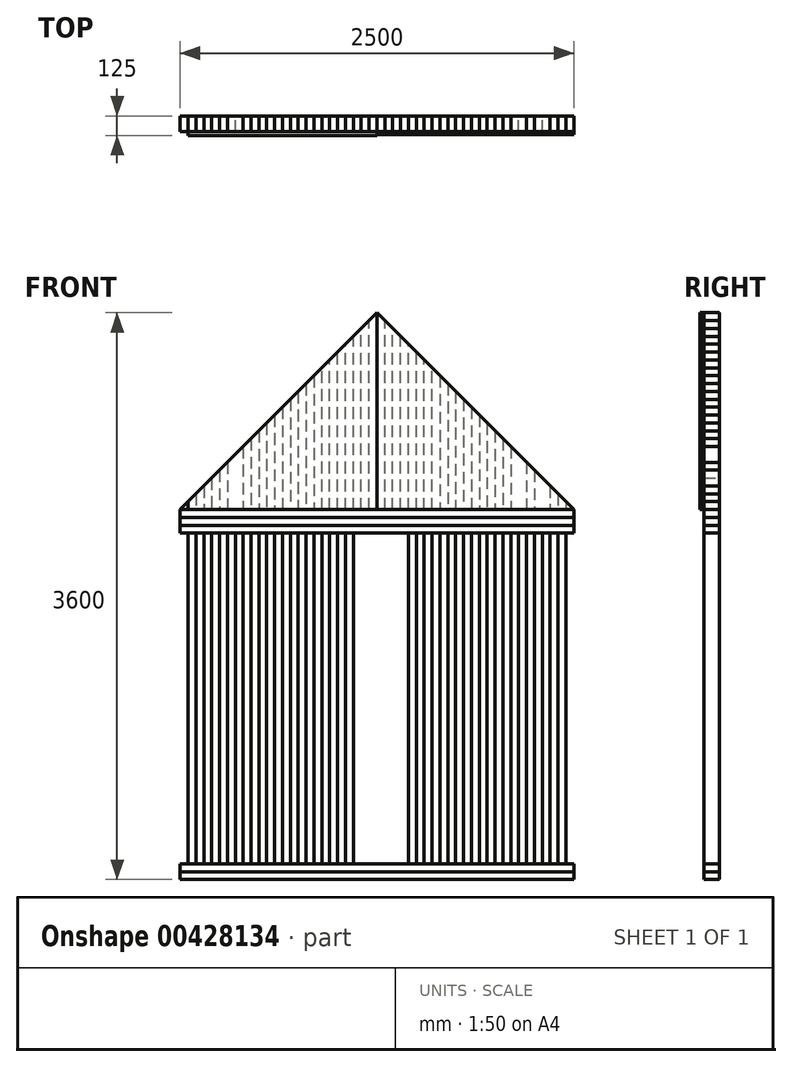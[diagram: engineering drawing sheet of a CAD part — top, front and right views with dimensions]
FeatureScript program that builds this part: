
annotation { "Feature Type Name" : "Feature", "Feature Type Description" : "" }
export const myFeature = defineFeature(function(context is Context, id is Id, definition is map)
    precondition{}
    {
        {
            var Q0;
            Q0=qCreatedBy(makeId("Front.planeOp"),FACE);
            var sketch = newSketch(context, id + "F0", { "sketchPlane" : qUnion([Q0])});
            skLineSegment(sketch, "E0.top", {"start": v(-1858, -1281.68) * mm, "end": v(642, -1281.68) * mm});
            skLineSegment(sketch, "E0.left", {"start": v(-1858, 1118.32) * mm, "end": v(-1858, -1281.68) * mm});
            skLineSegment(sketch, "E0.right", {"start": v(642, 1118.32) * mm, "end": v(642, -1281.68) * mm});
            skLineSegment(sketch, "E1", {"start": v(-1858, 1118.32) * mm, "end": v(-608, 2368.32) * mm});
            skLineSegment(sketch, "E2", {"start": v(-608, 2368.32) * mm, "end": v(642, 1118.32) * mm});
            skLineSegment(sketch, "E3.left", {"start": v(-1858, 1118.32) * mm, "end": v(-1858, 968.32) * mm});
            skLineSegment(sketch, "E3.right", {"start": v(642, 1118.32) * mm, "end": v(642, 968.32) * mm});
            skLineSegment(sketch, "E4", {"start": v(-1858, 1118.32) * mm, "end": v(642, 1118.32) * mm});
            skLineSegment(sketch, "E5", {"start": v(-608, 1118.32) * mm, "end": v(-608, 2368.32) * mm, "construction": true});
            skLineSegment(sketch, "E6", {"start": v(-608, 1118.32) * mm, "end": v(-658, 1118.32) * mm});
            skLineSegment(sketch, "E7", {"start": v(-658, 1118.32) * mm, "end": v(-658, 2318.32) * mm});
            skLineSegment(sketch, "E8", {"start": v(-708, 1118.32) * mm, "end": v(-708, 2268.32) * mm});
            skLineSegment(sketch, "E9", {"start": v(-758, 1118.32) * mm, "end": v(-758, 2218.32) * mm});
            skLineSegment(sketch, "E10", {"start": v(-808, 1118.32) * mm, "end": v(-808, 2168.32) * mm});
            skLineSegment(sketch, "E11", {"start": v(-858, 1118.32) * mm, "end": v(-858, 2118.32) * mm});
            skLineSegment(sketch, "E12", {"start": v(-908, 1118.32) * mm, "end": v(-908, 2068.32) * mm});
            skLineSegment(sketch, "E13", {"start": v(-958, 1118.32) * mm, "end": v(-958, 2018.32) * mm});
            skLineSegment(sketch, "E14", {"start": v(-1058, 1918.32) * mm, "end": v(-1058, 1118.32) * mm});
            skLineSegment(sketch, "E15", {"start": v(-1008, 1968.32) * mm, "end": v(-1008, 1118.32) * mm});
            skLineSegment(sketch, "E16", {"start": v(-1108, 1868.32) * mm, "end": v(-1108, 1118.32) * mm});
            skLineSegment(sketch, "E17", {"start": v(-1158, 1818.32) * mm, "end": v(-1158, 1118.32) * mm});
            skLineSegment(sketch, "E18", {"start": v(-1208, 1768.32) * mm, "end": v(-1208, 1118.32) * mm});
            skLineSegment(sketch, "E19", {"start": v(-1258, 1718.32) * mm, "end": v(-1258, 1118.32) * mm});
            skLineSegment(sketch, "E20", {"start": v(-1308, 1668.32) * mm, "end": v(-1308, 1118.32) * mm});
            skLineSegment(sketch, "E21", {"start": v(-1358, 1618.32) * mm, "end": v(-1358, 1118.32) * mm});
            skLineSegment(sketch, "E22", {"start": v(-1408, 1568.32) * mm, "end": v(-1408, 1118.32) * mm});
            skLineSegment(sketch, "E23", {"start": v(-1458, 1518.32) * mm, "end": v(-1458, 1118.32) * mm});
            skLineSegment(sketch, "E24", {"start": v(-1508, 1468.32) * mm, "end": v(-1508, 1118.32) * mm});
            skLineSegment(sketch, "E25", {"start": v(-1558, 1418.32) * mm, "end": v(-1558, 1118.32) * mm});
            skLineSegment(sketch, "E26", {"start": v(-1608, 1368.32) * mm, "end": v(-1608, 1118.32) * mm});
            skLineSegment(sketch, "E27", {"start": v(-1658, 1318.32) * mm, "end": v(-1658, 1118.32) * mm});
            skLineSegment(sketch, "E28", {"start": v(-1708, 1268.32) * mm, "end": v(-1708, 1118.32) * mm});
            skLineSegment(sketch, "E29", {"start": v(-1758, 1218.32) * mm, "end": v(-1758, 1118.32) * mm});
            skLineSegment(sketch, "E30", {"start": v(-1808, 1168.32) * mm, "end": v(-1808, 1118.32) * mm});
            skLineSegment(sketch, "E31.MirrorCS", {"start": v(-608, 1118.32) * mm, "end": v(-558, 1118.32) * mm});
            skLineSegment(sketch, "E32.MirrorCS", {"start": v(-158, 1918.32) * mm, "end": v(-158, 1118.32) * mm});
            skLineSegment(sketch, "E33.MirrorCS", {"start": v(592, 1168.32) * mm, "end": v(592, 1118.32) * mm});
            skLineSegment(sketch, "E34.MirrorCS", {"start": v(642, 1118.32) * mm, "end": v(-608, 2368.32) * mm});
            skLineSegment(sketch, "E35.MirrorCS", {"start": v(542, 1218.32) * mm, "end": v(542, 1118.32) * mm});
            skLineSegment(sketch, "E36.MirrorCS", {"start": v(292, 1468.32) * mm, "end": v(292, 1118.32) * mm});
            skLineSegment(sketch, "E37.MirrorCS", {"start": v(342, 1418.32) * mm, "end": v(342, 1118.32) * mm});
            skLineSegment(sketch, "E38.MirrorCS", {"start": v(242, 1518.32) * mm, "end": v(242, 1118.32) * mm});
            skLineSegment(sketch, "E39.MirrorCS", {"start": v(442, 1318.32) * mm, "end": v(442, 1118.32) * mm});
            skLineSegment(sketch, "E40.MirrorCS", {"start": v(192, 1568.32) * mm, "end": v(192, 1118.32) * mm});
            skLineSegment(sketch, "E41.MirrorCS", {"start": v(492, 1268.32) * mm, "end": v(492, 1118.32) * mm});
            skLineSegment(sketch, "E42.MirrorCS", {"start": v(-408, 1118.32) * mm, "end": v(-408, 2168.32) * mm});
            skLineSegment(sketch, "E43.MirrorCS", {"start": v(-358, 1118.32) * mm, "end": v(-358, 2118.32) * mm});
            skLineSegment(sketch, "E44.MirrorCS", {"start": v(-208, 1968.32) * mm, "end": v(-208, 1118.32) * mm});
            skLineSegment(sketch, "E45.MirrorCS", {"start": v(-8, 1768.32) * mm, "end": v(-8, 1118.32) * mm});
            skLineSegment(sketch, "E46.MirrorCS", {"start": v(142, 1618.32) * mm, "end": v(142, 1118.32) * mm});
            skLineSegment(sketch, "E47.MirrorCS", {"start": v(392, 1368.32) * mm, "end": v(392, 1118.32) * mm});
            skLineSegment(sketch, "E48.MirrorCS", {"start": v(642, 1118.32) * mm, "end": v(-1858, 1118.32) * mm});
            skLineSegment(sketch, "E49.MirrorCS", {"start": v(-558, 1118.32) * mm, "end": v(-558, 2318.32) * mm});
            skLineSegment(sketch, "E50.MirrorCS", {"start": v(-308, 1118.32) * mm, "end": v(-308, 2068.32) * mm});
            skLineSegment(sketch, "E51.MirrorCS", {"start": v(-508, 1118.32) * mm, "end": v(-508, 2268.32) * mm});
            skLineSegment(sketch, "E52.MirrorCS", {"start": v(-58, 1818.32) * mm, "end": v(-58, 1118.32) * mm});
            skLineSegment(sketch, "E53.MirrorCS", {"start": v(92, 1668.32) * mm, "end": v(92, 1118.32) * mm});
            skLineSegment(sketch, "E54.MirrorCS", {"start": v(-458, 1118.32) * mm, "end": v(-458, 2218.32) * mm});
            skLineSegment(sketch, "E55.MirrorCS", {"start": v(42, 1718.32) * mm, "end": v(42, 1118.32) * mm});
            skLineSegment(sketch, "E56.MirrorCS", {"start": v(-108, 1868.32) * mm, "end": v(-108, 1118.32) * mm});
            skLineSegment(sketch, "E57.MirrorCS", {"start": v(-258, 1118.32) * mm, "end": v(-258, 2018.32) * mm});
            skLineSegment(sketch, "E58.top", {"start": v(-1858, 968.32) * mm, "end": v(642, 968.32) * mm});
            skLineSegment(sketch, "E59.top", {"start": v(-1858, -1131.68) * mm, "end": v(642, -1131.68) * mm});
            skLineSegment(sketch, "E59.left", {"start": v(-1858, -1281.68) * mm, "end": v(-1858, -1131.68) * mm});
            skLineSegment(sketch, "E59.right", {"start": v(642, -1281.68) * mm, "end": v(642, -1131.68) * mm});
            skLineSegment(sketch, "E60.bottom", {"start": v(-1858, 968.32) * mm, "end": v(-1708, 968.32) * mm});
            skLineSegment(sketch, "E60.top", {"start": v(-1858, -1131.68) * mm, "end": v(-1708, -1131.68) * mm});
            skLineSegment(sketch, "E60.left", {"start": v(-1858, 968.32) * mm, "end": v(-1858, -1131.68) * mm});
            skLineSegment(sketch, "E60.right", {"start": v(-1708, 968.32) * mm, "end": v(-1708, -1131.68) * mm});
            skLineSegment(sketch, "E61.bottom", {"start": v(642, 968.32) * mm, "end": v(492, 968.32) * mm});
            skLineSegment(sketch, "E61.top", {"start": v(642, -1131.68) * mm, "end": v(492, -1131.68) * mm});
            skLineSegment(sketch, "E61.left", {"start": v(642, 968.32) * mm, "end": v(642, -1131.68) * mm});
            skLineSegment(sketch, "E61.right", {"start": v(492, 968.32) * mm, "end": v(492, -1131.68) * mm});
            skLineSegment(sketch, "E62", {"start": v(-1858, 1068.32) * mm, "end": v(642, 1068.32) * mm});
            skPoint(sketch, "E62.endSnap0", {"position": v(642, 1043.32) * mm});
            skLineSegment(sketch, "E63", {"start": v(-1858, 1018.32) * mm, "end": v(642, 1018.32) * mm});
            skLineSegment(sketch, "E64", {"start": v(-1808, 968.32) * mm, "end": v(-1808, -1131.68) * mm});
            skLineSegment(sketch, "E65", {"start": v(-1758, 968.32) * mm, "end": v(-1758, -1131.68) * mm});
            skLineSegment(sketch, "E66", {"start": v(-1858, -1181.68) * mm, "end": v(642, -1181.68) * mm});
            skPoint(sketch, "E66.endSnap0", {"position": v(642, -1206.68) * mm});
            skLineSegment(sketch, "E67", {"start": v(-1858, -1231.68) * mm, "end": v(642, -1231.68) * mm});
            skLineSegment(sketch, "E68", {"start": v(542, 968.32) * mm, "end": v(542, -1131.68) * mm});
            skLineSegment(sketch, "E69", {"start": v(592, 968.32) * mm, "end": v(592, -1131.68) * mm});
            skLineSegment(sketch, "E70", {"start": v(-1658, 968.32) * mm, "end": v(-1658, -1131.68) * mm});
            skLineSegment(sketch, "E71.1.0.0", {"start": v(-1608, 968.32) * mm, "end": v(-1608, -1131.68) * mm});
            skLineSegment(sketch, "E71.2.0.0", {"start": v(-1558, 968.32) * mm, "end": v(-1558, -1131.68) * mm});
            skLineSegment(sketch, "E71.3.0.0", {"start": v(-1508, 968.32) * mm, "end": v(-1508, -1131.68) * mm});
            skLineSegment(sketch, "E71.4.0.0", {"start": v(-1458, 968.32) * mm, "end": v(-1458, -1131.68) * mm});
            skLineSegment(sketch, "E71.5.0.0", {"start": v(-1408, 968.32) * mm, "end": v(-1408, -1131.68) * mm});
            skLineSegment(sketch, "E71.6.0.0", {"start": v(-1358, 968.32) * mm, "end": v(-1358, -1131.68) * mm});
            skLineSegment(sketch, "E71.7.0.0", {"start": v(-1308, 968.32) * mm, "end": v(-1308, -1131.68) * mm});
            skLineSegment(sketch, "E71.8.0.0", {"start": v(-1258, 968.32) * mm, "end": v(-1258, -1131.68) * mm});
            skLineSegment(sketch, "E71.9.0.0", {"start": v(-1208, 968.32) * mm, "end": v(-1208, -1131.68) * mm});
            skLineSegment(sketch, "E71.direction1", {"start": v(-1658, -1131.68) * mm, "end": v(-1608, -1131.68) * mm, "construction": true});
            skLineSegment(sketch, "E72.1.0.0", {"start": v(442, 968.32) * mm, "end": v(442, -1131.68) * mm});
            skLineSegment(sketch, "E72.2.0.0", {"start": v(392, 968.32) * mm, "end": v(392, -1131.68) * mm});
            skLineSegment(sketch, "E72.3.0.0", {"start": v(342, 968.32) * mm, "end": v(342, -1131.68) * mm});
            skLineSegment(sketch, "E72.4.0.0", {"start": v(292, 968.32) * mm, "end": v(292, -1131.68) * mm});
            skLineSegment(sketch, "E72.5.0.0", {"start": v(242, 968.32) * mm, "end": v(242, -1131.68) * mm});
            skLineSegment(sketch, "E72.6.0.0", {"start": v(192, 968.32) * mm, "end": v(192, -1131.68) * mm});
            skLineSegment(sketch, "E72.7.0.0", {"start": v(142, 968.32) * mm, "end": v(142, -1131.68) * mm});
            skLineSegment(sketch, "E72.8.0.0", {"start": v(92, 968.32) * mm, "end": v(92, -1131.68) * mm});
            skLineSegment(sketch, "E72.9.0.0", {"start": v(42, 968.32) * mm, "end": v(42, -1131.68) * mm});
            skLineSegment(sketch, "E72.direction1", {"start": v(492, -1131.68) * mm, "end": v(442, -1131.68) * mm, "construction": true});
            skLineSegment(sketch, "E73.1.0.0", {"start": v(-1158, 968.32) * mm, "end": v(-1158, -1131.68) * mm});
            skLineSegment(sketch, "E73.2.0.0", {"start": v(-1108, 968.32) * mm, "end": v(-1108, -1131.68) * mm});
            skLineSegment(sketch, "E73.3.0.0", {"start": v(-1058, 968.32) * mm, "end": v(-1058, -1131.68) * mm});
            skLineSegment(sketch, "E73.4.0.0", {"start": v(-1008, 968.32) * mm, "end": v(-1008, -1131.68) * mm});
            skLineSegment(sketch, "E73.5.0.0", {"start": v(-958, 968.32) * mm, "end": v(-958, -1131.68) * mm});
            skLineSegment(sketch, "E73.6.0.0", {"start": v(-908, 968.32) * mm, "end": v(-908, -1131.68) * mm});
            skLineSegment(sketch, "E73.7.0.0", {"start": v(-858, 968.32) * mm, "end": v(-858, -1131.68) * mm});
            skLineSegment(sketch, "E73.8.0.0", {"start": v(-808, 968.32) * mm, "end": v(-808, -1131.68) * mm});
            skLineSegment(sketch, "E73.9.0.0", {"start": v(-758, 968.32) * mm, "end": v(-758, -1131.68) * mm});
            skLineSegment(sketch, "E73.direction1", {"start": v(-1208, -1131.68) * mm, "end": v(-1158, -1131.68) * mm, "construction": true});
            skLineSegment(sketch, "E74.1.0.0", {"start": v(-8, 968.32) * mm, "end": v(-8, -1131.68) * mm});
            skLineSegment(sketch, "E74.2.0.0", {"start": v(-58, 968.32) * mm, "end": v(-58, -1131.68) * mm});
            skLineSegment(sketch, "E74.3.0.0", {"start": v(-108, 968.32) * mm, "end": v(-108, -1131.68) * mm});
            skLineSegment(sketch, "E74.4.0.0", {"start": v(-158, 968.32) * mm, "end": v(-158, -1131.68) * mm});
            skLineSegment(sketch, "E74.5.0.0", {"start": v(-208, 968.32) * mm, "end": v(-208, -1131.68) * mm});
            skLineSegment(sketch, "E74.6.0.0", {"start": v(-258, 968.32) * mm, "end": v(-258, -1131.68) * mm});
            skLineSegment(sketch, "E74.7.0.0", {"start": v(-308, 968.32) * mm, "end": v(-308, -1131.68) * mm});
            skLineSegment(sketch, "E74.8.0.0", {"start": v(-358, 968.32) * mm, "end": v(-358, -1131.68) * mm});
            skLineSegment(sketch, "E74.9.0.0", {"start": v(-408, 968.32) * mm, "end": v(-408, -1131.68) * mm});
            skLineSegment(sketch, "E74.direction1", {"start": v(42, -1131.68) * mm, "end": v(-8, -1131.68) * mm, "construction": true});
            skSolve(sketch);
        }
        {
            var Q0;
            {var subQ3=sQuery(id+"F0.wireOp",EDGE,"E30");Q0=makeQuery(id+"F0.imprint","IMPRINT",FACE,{"disambiguationData":[TD([[makeQuery(id+"F0.imprint","IMPRINT",EDGE,{"derivedFrom":subQ3}),-1.0]])]});}
            var Q1;
            {var subQ0=sQuery(id+"F0.wireOp",EDGE,"E28");Q1=makeQuery(id+"F0.imprint","IMPRINT",FACE,{"disambiguationData":[TD([[makeQuery(id+"F0.imprint","IMPRINT",EDGE,{"derivedFrom":subQ0}),-1.0]])]});}
            var Q2;
            {var subQ0=sQuery(id+"F0.wireOp",EDGE,"E26");Q2=makeQuery(id+"F0.imprint","IMPRINT",FACE,{"disambiguationData":[TD([[makeQuery(id+"F0.imprint","IMPRINT",EDGE,{"derivedFrom":subQ0}),-1.0]])]});}
            var Q3;
            {var subQ0=sQuery(id+"F0.wireOp",EDGE,"E24");Q3=makeQuery(id+"F0.imprint","IMPRINT",FACE,{"disambiguationData":[TD([[makeQuery(id+"F0.imprint","IMPRINT",EDGE,{"derivedFrom":subQ0}),-1.0]])]});}
            var Q4;
            {var subQ0=sQuery(id+"F0.wireOp",EDGE,"E22");Q4=makeQuery(id+"F0.imprint","IMPRINT",FACE,{"disambiguationData":[TD([[makeQuery(id+"F0.imprint","IMPRINT",EDGE,{"derivedFrom":subQ0}),-1.0]])]});}
            var Q5;
            {var subQ0=sQuery(id+"F0.wireOp",EDGE,"E20");Q5=makeQuery(id+"F0.imprint","IMPRINT",FACE,{"disambiguationData":[TD([[makeQuery(id+"F0.imprint","IMPRINT",EDGE,{"derivedFrom":subQ0}),-1.0]])]});}
            var Q6;
            {var subQ0=sQuery(id+"F0.wireOp",EDGE,"E18");Q6=makeQuery(id+"F0.imprint","IMPRINT",FACE,{"disambiguationData":[TD([[makeQuery(id+"F0.imprint","IMPRINT",EDGE,{"derivedFrom":subQ0}),-1.0]])]});}
            var Q7;
            {var subQ0=sQuery(id+"F0.wireOp",EDGE,"E16");Q7=makeQuery(id+"F0.imprint","IMPRINT",FACE,{"disambiguationData":[TD([[makeQuery(id+"F0.imprint","IMPRINT",EDGE,{"derivedFrom":subQ0}),-1.0]])]});}
            var Q8;
            {var subQ0=sQuery(id+"F0.wireOp",EDGE,"E15");Q8=makeQuery(id+"F0.imprint","IMPRINT",FACE,{"disambiguationData":[TD([[makeQuery(id+"F0.imprint","IMPRINT",EDGE,{"derivedFrom":subQ0}),-1.0]])]});}
            var Q9;
            {var subQ0=sQuery(id+"F0.wireOp",EDGE,"E12");Q9=makeQuery(id+"F0.imprint","IMPRINT",FACE,{"disambiguationData":[TD([[makeQuery(id+"F0.imprint","IMPRINT",EDGE,{"derivedFrom":subQ0}),1.0]])]});}
            var Q10;
            {var subQ0=sQuery(id+"F0.wireOp",EDGE,"E10");Q10=makeQuery(id+"F0.imprint","IMPRINT",FACE,{"disambiguationData":[TD([[makeQuery(id+"F0.imprint","IMPRINT",EDGE,{"derivedFrom":subQ0}),1.0]])]});}
            var Q11;
            {var subQ0=sQuery(id+"F0.wireOp",EDGE,"E8");Q11=makeQuery(id+"F0.imprint","IMPRINT",FACE,{"disambiguationData":[TD([[makeQuery(id+"F0.imprint","IMPRINT",EDGE,{"derivedFrom":subQ0}),1.0]])]});}
            var Q12;
            {var subQ1=sQuery(id+"F0.wireOp",EDGE,"E7");Q12=makeQuery(id+"F0.imprint","IMPRINT",FACE,{"disambiguationData":[TD([[makeQuery(id+"F0.imprint","IMPRINT",EDGE,{"derivedFrom":subQ1}),-1.0]])]});}
            var Q13;
            {var subQ0=sQuery(id+"F0.wireOp",EDGE,"E51.MirrorCS");Q13=makeQuery(id+"F0.imprint","IMPRINT",FACE,{"disambiguationData":[TD([[makeQuery(id+"F0.imprint","IMPRINT",EDGE,{"derivedFrom":subQ0}),-1.0]])]});}
            var Q14;
            {var subQ0=sQuery(id+"F0.wireOp",EDGE,"E42.MirrorCS");Q14=makeQuery(id+"F0.imprint","IMPRINT",FACE,{"disambiguationData":[TD([[makeQuery(id+"F0.imprint","IMPRINT",EDGE,{"derivedFrom":subQ0}),-1.0]])]});}
            var Q15;
            {var subQ0=sQuery(id+"F0.wireOp",EDGE,"E50.MirrorCS");Q15=makeQuery(id+"F0.imprint","IMPRINT",FACE,{"disambiguationData":[TD([[makeQuery(id+"F0.imprint","IMPRINT",EDGE,{"derivedFrom":subQ0}),-1.0]])]});}
            var Q16;
            {var subQ0=sQuery(id+"F0.wireOp",EDGE,"E44.MirrorCS");Q16=makeQuery(id+"F0.imprint","IMPRINT",FACE,{"disambiguationData":[TD([[makeQuery(id+"F0.imprint","IMPRINT",EDGE,{"derivedFrom":subQ0}),1.0]])]});}
            var Q17;
            {var subQ0=sQuery(id+"F0.wireOp",EDGE,"E52.MirrorCS");Q17=makeQuery(id+"F0.imprint","IMPRINT",FACE,{"disambiguationData":[TD([[makeQuery(id+"F0.imprint","IMPRINT",EDGE,{"derivedFrom":subQ0}),-1.0]])]});}
            var Q18;
            {var subQ0=sQuery(id+"F0.wireOp",EDGE,"E45.MirrorCS");Q18=makeQuery(id+"F0.imprint","IMPRINT",FACE,{"disambiguationData":[TD([[makeQuery(id+"F0.imprint","IMPRINT",EDGE,{"derivedFrom":subQ0}),1.0]])]});}
            var Q19;
            {var subQ0=sQuery(id+"F0.wireOp",EDGE,"E46.MirrorCS");Q19=makeQuery(id+"F0.imprint","IMPRINT",FACE,{"disambiguationData":[TD([[makeQuery(id+"F0.imprint","IMPRINT",EDGE,{"derivedFrom":subQ0}),-1.0]])]});}
            var Q20;
            {var subQ0=sQuery(id+"F0.wireOp",EDGE,"E40.MirrorCS");Q20=makeQuery(id+"F0.imprint","IMPRINT",FACE,{"disambiguationData":[TD([[makeQuery(id+"F0.imprint","IMPRINT",EDGE,{"derivedFrom":subQ0}),1.0]])]});}
            var Q21;
            {var subQ0=sQuery(id+"F0.wireOp",EDGE,"E36.MirrorCS");Q21=makeQuery(id+"F0.imprint","IMPRINT",FACE,{"disambiguationData":[TD([[makeQuery(id+"F0.imprint","IMPRINT",EDGE,{"derivedFrom":subQ0}),1.0]])]});}
            var Q22;
            {var subQ0=sQuery(id+"F0.wireOp",EDGE,"E39.MirrorCS");Q22=makeQuery(id+"F0.imprint","IMPRINT",FACE,{"disambiguationData":[TD([[makeQuery(id+"F0.imprint","IMPRINT",EDGE,{"derivedFrom":subQ0}),-1.0]])]});}
            var Q23;
            {var subQ0=sQuery(id+"F0.wireOp",EDGE,"E35.MirrorCS");Q23=makeQuery(id+"F0.imprint","IMPRINT",FACE,{"disambiguationData":[TD([[makeQuery(id+"F0.imprint","IMPRINT",EDGE,{"derivedFrom":subQ0}),-1.0]])]});}
            var Q24;
            {var subQ0=sQuery(id+"F0.wireOp",EDGE,"E33.MirrorCS");Q24=makeQuery(id+"F0.imprint","IMPRINT",FACE,{"disambiguationData":[TD([[makeQuery(id+"F0.imprint","IMPRINT",EDGE,{"derivedFrom":subQ0}),1.0]])]});}
            extrude(context, id + "F1", {"entities" : qUnion([Q0, Q1, Q2, Q3, Q4, Q5, Q6, Q7, Q8, Q9, Q10, Q11, Q12, Q13, Q14, Q15, Q16, Q17, Q18, Q19, Q20, Q21, Q22, Q23, Q24]), "depth" : 100 * mm});
        }
        {
            var Q0;
            {var subQ0=sQuery(id+"F0.wireOp",EDGE,"E29");Q0=makeQuery(id+"F0.imprint","IMPRINT",FACE,{"disambiguationData":[TD([[makeQuery(id+"F0.imprint","IMPRINT",EDGE,{"derivedFrom":subQ0}),-1.0]])]});}
            var Q1;
            {var subQ0=sQuery(id+"F0.wireOp",EDGE,"E28");Q1=makeQuery(id+"F0.imprint","IMPRINT",FACE,{"disambiguationData":[TD([[makeQuery(id+"F0.imprint","IMPRINT",EDGE,{"derivedFrom":subQ0}),1.0]])]});}
            var Q2;
            {var subQ0=sQuery(id+"F0.wireOp",EDGE,"E25");Q2=makeQuery(id+"F0.imprint","IMPRINT",FACE,{"disambiguationData":[TD([[makeQuery(id+"F0.imprint","IMPRINT",EDGE,{"derivedFrom":subQ0}),-1.0]])]});}
            var Q3;
            {var subQ0=sQuery(id+"F0.wireOp",EDGE,"E23");Q3=makeQuery(id+"F0.imprint","IMPRINT",FACE,{"disambiguationData":[TD([[makeQuery(id+"F0.imprint","IMPRINT",EDGE,{"derivedFrom":subQ0}),-1.0]])]});}
            var Q4;
            {var subQ0=sQuery(id+"F0.wireOp",EDGE,"E21");Q4=makeQuery(id+"F0.imprint","IMPRINT",FACE,{"disambiguationData":[TD([[makeQuery(id+"F0.imprint","IMPRINT",EDGE,{"derivedFrom":subQ0}),-1.0]])]});}
            var Q5;
            {var subQ0=sQuery(id+"F0.wireOp",EDGE,"E19");Q5=makeQuery(id+"F0.imprint","IMPRINT",FACE,{"disambiguationData":[TD([[makeQuery(id+"F0.imprint","IMPRINT",EDGE,{"derivedFrom":subQ0}),-1.0]])]});}
            var Q6;
            {var subQ0=sQuery(id+"F0.wireOp",EDGE,"E17");Q6=makeQuery(id+"F0.imprint","IMPRINT",FACE,{"disambiguationData":[TD([[makeQuery(id+"F0.imprint","IMPRINT",EDGE,{"derivedFrom":subQ0}),-1.0]])]});}
            var Q7;
            {var subQ0=sQuery(id+"F0.wireOp",EDGE,"E14");Q7=makeQuery(id+"F0.imprint","IMPRINT",FACE,{"disambiguationData":[TD([[makeQuery(id+"F0.imprint","IMPRINT",EDGE,{"derivedFrom":subQ0}),-1.0]])]});}
            var Q8;
            {var subQ0=sQuery(id+"F0.wireOp",EDGE,"E13");Q8=makeQuery(id+"F0.imprint","IMPRINT",FACE,{"disambiguationData":[TD([[makeQuery(id+"F0.imprint","IMPRINT",EDGE,{"derivedFrom":subQ0}),1.0]])]});}
            var Q9;
            {var subQ0=sQuery(id+"F0.wireOp",EDGE,"E11");Q9=makeQuery(id+"F0.imprint","IMPRINT",FACE,{"disambiguationData":[TD([[makeQuery(id+"F0.imprint","IMPRINT",EDGE,{"derivedFrom":subQ0}),1.0]])]});}
            var Q10;
            {var subQ0=sQuery(id+"F0.wireOp",EDGE,"E9");Q10=makeQuery(id+"F0.imprint","IMPRINT",FACE,{"disambiguationData":[TD([[makeQuery(id+"F0.imprint","IMPRINT",EDGE,{"derivedFrom":subQ0}),1.0]])]});}
            var Q11;
            {var subQ0=sQuery(id+"F0.wireOp",EDGE,"E7");Q11=makeQuery(id+"F0.imprint","IMPRINT",FACE,{"disambiguationData":[TD([[makeQuery(id+"F0.imprint","IMPRINT",EDGE,{"derivedFrom":subQ0}),1.0]])]});}
            var Q12;
            {var subQ0=sQuery(id+"F0.wireOp",EDGE,"E49.MirrorCS");Q12=makeQuery(id+"F0.imprint","IMPRINT",FACE,{"disambiguationData":[TD([[makeQuery(id+"F0.imprint","IMPRINT",EDGE,{"derivedFrom":subQ0}),-1.0]])]});}
            var Q13;
            {var subQ0=sQuery(id+"F0.wireOp",EDGE,"E42.MirrorCS");Q13=makeQuery(id+"F0.imprint","IMPRINT",FACE,{"disambiguationData":[TD([[makeQuery(id+"F0.imprint","IMPRINT",EDGE,{"derivedFrom":subQ0}),1.0]])]});}
            var Q14;
            {var subQ0=sQuery(id+"F0.wireOp",EDGE,"E43.MirrorCS");Q14=makeQuery(id+"F0.imprint","IMPRINT",FACE,{"disambiguationData":[TD([[makeQuery(id+"F0.imprint","IMPRINT",EDGE,{"derivedFrom":subQ0}),-1.0]])]});}
            var Q15;
            {var subQ0=sQuery(id+"F0.wireOp",EDGE,"E44.MirrorCS");Q15=makeQuery(id+"F0.imprint","IMPRINT",FACE,{"disambiguationData":[TD([[makeQuery(id+"F0.imprint","IMPRINT",EDGE,{"derivedFrom":subQ0}),-1.0]])]});}
            var Q16;
            {var subQ0=sQuery(id+"F0.wireOp",EDGE,"E32.MirrorCS");Q16=makeQuery(id+"F0.imprint","IMPRINT",FACE,{"disambiguationData":[TD([[makeQuery(id+"F0.imprint","IMPRINT",EDGE,{"derivedFrom":subQ0}),1.0]])]});}
            var Q17;
            {var subQ0=sQuery(id+"F0.wireOp",EDGE,"E45.MirrorCS");Q17=makeQuery(id+"F0.imprint","IMPRINT",FACE,{"disambiguationData":[TD([[makeQuery(id+"F0.imprint","IMPRINT",EDGE,{"derivedFrom":subQ0}),-1.0]])]});}
            var Q18;
            {var subQ0=sQuery(id+"F0.wireOp",EDGE,"E53.MirrorCS");Q18=makeQuery(id+"F0.imprint","IMPRINT",FACE,{"disambiguationData":[TD([[makeQuery(id+"F0.imprint","IMPRINT",EDGE,{"derivedFrom":subQ0}),-1.0]])]});}
            var Q19;
            {var subQ0=sQuery(id+"F0.wireOp",EDGE,"E40.MirrorCS");Q19=makeQuery(id+"F0.imprint","IMPRINT",FACE,{"disambiguationData":[TD([[makeQuery(id+"F0.imprint","IMPRINT",EDGE,{"derivedFrom":subQ0}),-1.0]])]});}
            var Q20;
            {var subQ0=sQuery(id+"F0.wireOp",EDGE,"E36.MirrorCS");Q20=makeQuery(id+"F0.imprint","IMPRINT",FACE,{"disambiguationData":[TD([[makeQuery(id+"F0.imprint","IMPRINT",EDGE,{"derivedFrom":subQ0}),-1.0]])]});}
            var Q21;
            {var subQ0=sQuery(id+"F0.wireOp",EDGE,"E37.MirrorCS");Q21=makeQuery(id+"F0.imprint","IMPRINT",FACE,{"disambiguationData":[TD([[makeQuery(id+"F0.imprint","IMPRINT",EDGE,{"derivedFrom":subQ0}),1.0]])]});}
            var Q22;
            {var subQ0=sQuery(id+"F0.wireOp",EDGE,"E39.MirrorCS");Q22=makeQuery(id+"F0.imprint","IMPRINT",FACE,{"disambiguationData":[TD([[makeQuery(id+"F0.imprint","IMPRINT",EDGE,{"derivedFrom":subQ0}),1.0]])]});}
            var Q23;
            {var subQ0=sQuery(id+"F0.wireOp",EDGE,"E33.MirrorCS");Q23=makeQuery(id+"F0.imprint","IMPRINT",FACE,{"disambiguationData":[TD([[makeQuery(id+"F0.imprint","IMPRINT",EDGE,{"derivedFrom":subQ0}),-1.0]])]});}
            extrude(context, id + "F2", {"entities" : qUnion([Q0, Q1, Q2, Q3, Q4, Q5, Q6, Q7, Q8, Q9, Q10, Q11, Q12, Q13, Q14, Q15, Q16, Q17, Q18, Q19, Q20, Q21, Q22, Q23]), "depth" : 100 * mm});
        }
        {
            var Q0;
            {var subQ0=sQuery(id+"F0.wireOp",EDGE,"E60.left");Q0=makeQuery(id+"F0.imprint","IMPRINT",FACE,{"disambiguationData":[TD([[makeQuery(id+"F0.imprint","IMPRINT",EDGE,{"derivedFrom":subQ0}),1.0]])]});}
            var Q1;
            {var subQ0=sQuery(id+"F0.wireOp",EDGE,"E60.right");Q1=makeQuery(id+"F0.imprint","IMPRINT",FACE,{"disambiguationData":[TD([[makeQuery(id+"F0.imprint","IMPRINT",EDGE,{"derivedFrom":subQ0}),-1.0]])]});}
            var Q2;
            {var subQ0=sQuery(id+"F0.wireOp",EDGE,"E66");Q2=makeQuery(id+"F0.imprint","IMPRINT",FACE,{"disambiguationData":[TD([[makeQuery(id+"F0.imprint","IMPRINT",EDGE,{"derivedFrom":subQ0}),-1.0]])]});}
            var Q3;
            {var subQ0=sQuery(id+"F0.wireOp",EDGE,"E61.right");Q3=makeQuery(id+"F0.imprint","IMPRINT",FACE,{"disambiguationData":[TD([[makeQuery(id+"F0.imprint","IMPRINT",EDGE,{"derivedFrom":subQ0}),1.0]])]});}
            var Q4;
            {var subQ0=sQuery(id+"F0.wireOp",EDGE,"E61.left");Q4=makeQuery(id+"F0.imprint","IMPRINT",FACE,{"disambiguationData":[TD([[makeQuery(id+"F0.imprint","IMPRINT",EDGE,{"derivedFrom":subQ0}),-1.0]])]});}
            var Q5;
            {var subQ0=sQuery(id+"F0.wireOp",EDGE,"E62");Q5=makeQuery(id+"F0.imprint","IMPRINT",FACE,{"disambiguationData":[TD([[makeQuery(id+"F0.imprint","IMPRINT",EDGE,{"derivedFrom":subQ0}),-1.0]])]});}
            extrude(context, id + "F3", {"entities" : qUnion([Q0, Q1, Q2, Q3, Q4, Q5]), "depth" : 100 * mm});
        }
        {
            var Q0;
            {var subQ53=sQuery(id+"F0.wireOp",EDGE,"E62");Q0=makeQuery(id+"F0.imprint","IMPRINT",FACE,{"disambiguationData":[TD([[makeQuery(id+"F0.imprint","IMPRINT",EDGE,{"derivedFrom":subQ53}),1.0]])]});}
            var Q1;
            {var subQ5=sQuery(id+"F0.wireOp",EDGE,"E58.top");Q1=makeQuery(id+"F0.imprint","IMPRINT",FACE,{"disambiguationData":[TD([[makeQuery(id+"F0.imprint","IMPRINT",EDGE,{"derivedFrom":subQ5}),1.0]])]});}
            var Q2;
            {var subQ8=sQuery(id+"F0.wireOp",EDGE,"E59.top");Q2=makeQuery(id+"F0.imprint","IMPRINT",FACE,{"disambiguationData":[TD([[makeQuery(id+"F0.imprint","IMPRINT",EDGE,{"derivedFrom":subQ8}),-1.0]])]});}
            var Q3;
            {var subQ0=sQuery(id+"F0.wireOp",EDGE,"E0.top");Q3=makeQuery(id+"F0.imprint","IMPRINT",FACE,{"disambiguationData":[TD([[makeQuery(id+"F0.imprint","IMPRINT",EDGE,{"derivedFrom":subQ0}),1.0]])]});}
            extrude(context, id + "F4", {"entities" : qUnion([Q0, Q1, Q2, Q3]), "depth" : 100 * mm});
        }
        {
            var Q0;
            Q0=makeQuery(id+"F1.opExtrude","CAP_FACE",FACE,{"disambiguationData":[OSD([sQuery(id+"F0.wireOp",EDGE,"E1"),sQuery(id+"F0.wireOp",EDGE,"E30"),sQuery(id+"F0.wireOp",EDGE,"E4")])],"isStart":false});
            var sketch = newSketch(context, id + "F5", { "sketchPlane" : qUnion([Q0])});
            skLineSegment(sketch, "E75.bottom", {"start": v(-1858, 1118.32) * mm, "end": v(642, 1118.32) * mm, "construction": true});
            skLineSegment(sketch, "E75.top", {"start": v(-1858, 2368.32) * mm, "end": v(642, 2368.32) * mm, "construction": true});
            skLineSegment(sketch, "E75.left", {"start": v(-1858, 1118.32) * mm, "end": v(-1858, 2368.32) * mm, "construction": true});
            skLineSegment(sketch, "E75.right", {"start": v(642, 1118.32) * mm, "end": v(642, 2368.32) * mm, "construction": true});
            skLineSegment(sketch, "E76", {"start": v(-1858, 1118.32) * mm, "end": v(-608, 2368.32) * mm});
            skLineSegment(sketch, "E77", {"start": v(-608, 2368.32) * mm, "end": v(-608, 1118.32) * mm});
            skLineSegment(sketch, "E78", {"start": v(-608, 1118.32) * mm, "end": v(-1858, 1118.32) * mm});
            skLineSegment(sketch, "E79", {"start": v(-608, 2368.32) * mm, "end": v(642, 1118.32) * mm});
            skLineSegment(sketch, "E80", {"start": v(-608, 1118.32) * mm, "end": v(642, 1118.32) * mm});
            skSolve(sketch);
        }
        {
            var Q0;
            {var subQ2=sQuery(id+"F5.wireOp",EDGE,"E77");Q0=makeQuery(id+"F5.imprint","IMPRINT",FACE,{"disambiguationData":[TD([[makeQuery(id+"F5.imprint","IMPRINT",EDGE,{"derivedFrom":subQ2}),-1.0]])]});}
            extrude(context, id + "F6", {"entities" : qUnion([Q0]), "depth" : 25 * mm});
        }
        {
            var Q0;
            Q0=makeQuery(id+"F5.imprint","IMPRINT",FACE,{"disambiguationData":[TD([[makeQuery(id+"F5.imprint","IMPRINT",EDGE,{"derivedFrom":sQuery(id+"F5.wireOp",EDGE,"E77")}),1.0]])]});
            extrude(context, id + "F7", {"entities" : qUnion([Q0]), "depth" : 18 * mm});
        }
        {
            var Q0;
            {var subQ0=sQuery(id+"F0.wireOp",EDGE,"E64");Q0=makeQuery(id+"F0.imprint","IMPRINT",FACE,{"disambiguationData":[TD([[makeQuery(id+"F0.imprint","IMPRINT",EDGE,{"derivedFrom":subQ0}),1.0]])]});}
            var Q1;
            {var subQ0=sQuery(id+"F0.wireOp",EDGE,"E60.right");Q1=makeQuery(id+"F0.imprint","IMPRINT",FACE,{"disambiguationData":[TD([[makeQuery(id+"F0.imprint","IMPRINT",EDGE,{"derivedFrom":subQ0}),1.0]])]});}
            var Q2;
            {var subQ0=sQuery(id+"F0.wireOp",EDGE,"E71.1.0.0");Q2=makeQuery(id+"F0.imprint","IMPRINT",FACE,{"disambiguationData":[TD([[makeQuery(id+"F0.imprint","IMPRINT",EDGE,{"derivedFrom":subQ0}),1.0]])]});}
            var Q3;
            {var subQ0=sQuery(id+"F0.wireOp",EDGE,"E71.3.0.0");Q3=makeQuery(id+"F0.imprint","IMPRINT",FACE,{"disambiguationData":[TD([[makeQuery(id+"F0.imprint","IMPRINT",EDGE,{"derivedFrom":subQ0}),1.0]])]});}
            var Q4;
            {var subQ0=sQuery(id+"F0.wireOp",EDGE,"E71.5.0.0");Q4=makeQuery(id+"F0.imprint","IMPRINT",FACE,{"disambiguationData":[TD([[makeQuery(id+"F0.imprint","IMPRINT",EDGE,{"derivedFrom":subQ0}),1.0]])]});}
            var Q5;
            {var subQ0=sQuery(id+"F0.wireOp",EDGE,"E71.7.0.0");Q5=makeQuery(id+"F0.imprint","IMPRINT",FACE,{"disambiguationData":[TD([[makeQuery(id+"F0.imprint","IMPRINT",EDGE,{"derivedFrom":subQ0}),1.0]])]});}
            var Q6;
            {var subQ0=sQuery(id+"F0.wireOp",EDGE,"E71.9.0.0");Q6=makeQuery(id+"F0.imprint","IMPRINT",FACE,{"disambiguationData":[TD([[makeQuery(id+"F0.imprint","IMPRINT",EDGE,{"derivedFrom":subQ0}),1.0]])]});}
            var Q7;
            {var subQ0=sQuery(id+"F0.wireOp",EDGE,"E73.2.0.0");Q7=makeQuery(id+"F0.imprint","IMPRINT",FACE,{"disambiguationData":[TD([[makeQuery(id+"F0.imprint","IMPRINT",EDGE,{"derivedFrom":subQ0}),1.0]])]});}
            var Q8;
            {var subQ0=sQuery(id+"F0.wireOp",EDGE,"E73.4.0.0");Q8=makeQuery(id+"F0.imprint","IMPRINT",FACE,{"disambiguationData":[TD([[makeQuery(id+"F0.imprint","IMPRINT",EDGE,{"derivedFrom":subQ0}),1.0]])]});}
            var Q9;
            {var subQ0=sQuery(id+"F0.wireOp",EDGE,"E73.6.0.0");Q9=makeQuery(id+"F0.imprint","IMPRINT",FACE,{"disambiguationData":[TD([[makeQuery(id+"F0.imprint","IMPRINT",EDGE,{"derivedFrom":subQ0}),1.0]])]});}
            var Q10;
            {var subQ0=sQuery(id+"F0.wireOp",EDGE,"E73.8.0.0");Q10=makeQuery(id+"F0.imprint","IMPRINT",FACE,{"disambiguationData":[TD([[makeQuery(id+"F0.imprint","IMPRINT",EDGE,{"derivedFrom":subQ0}),1.0]])]});}
            var Q11;
            {var subQ0=sQuery(id+"F0.wireOp",EDGE,"E68");Q11=makeQuery(id+"F0.imprint","IMPRINT",FACE,{"disambiguationData":[TD([[makeQuery(id+"F0.imprint","IMPRINT",EDGE,{"derivedFrom":subQ0}),1.0]])]});}
            var Q12;
            {var subQ0=sQuery(id+"F0.wireOp",EDGE,"E61.right");Q12=makeQuery(id+"F0.imprint","IMPRINT",FACE,{"disambiguationData":[TD([[makeQuery(id+"F0.imprint","IMPRINT",EDGE,{"derivedFrom":subQ0}),-1.0]])]});}
            var Q13;
            {var subQ0=sQuery(id+"F0.wireOp",EDGE,"E72.2.0.0");Q13=makeQuery(id+"F0.imprint","IMPRINT",FACE,{"disambiguationData":[TD([[makeQuery(id+"F0.imprint","IMPRINT",EDGE,{"derivedFrom":subQ0}),-1.0]])]});}
            var Q14;
            {var subQ0=sQuery(id+"F0.wireOp",EDGE,"E72.4.0.0");Q14=makeQuery(id+"F0.imprint","IMPRINT",FACE,{"disambiguationData":[TD([[makeQuery(id+"F0.imprint","IMPRINT",EDGE,{"derivedFrom":subQ0}),-1.0]])]});}
            var Q15;
            {var subQ0=sQuery(id+"F0.wireOp",EDGE,"E72.6.0.0");Q15=makeQuery(id+"F0.imprint","IMPRINT",FACE,{"disambiguationData":[TD([[makeQuery(id+"F0.imprint","IMPRINT",EDGE,{"derivedFrom":subQ0}),-1.0]])]});}
            var Q16;
            {var subQ0=sQuery(id+"F0.wireOp",EDGE,"E72.8.0.0");Q16=makeQuery(id+"F0.imprint","IMPRINT",FACE,{"disambiguationData":[TD([[makeQuery(id+"F0.imprint","IMPRINT",EDGE,{"derivedFrom":subQ0}),-1.0]])]});}
            var Q17;
            {var subQ0=sQuery(id+"F0.wireOp",EDGE,"E74.1.0.0");Q17=makeQuery(id+"F0.imprint","IMPRINT",FACE,{"disambiguationData":[TD([[makeQuery(id+"F0.imprint","IMPRINT",EDGE,{"derivedFrom":subQ0}),-1.0]])]});}
            var Q18;
            {var subQ0=sQuery(id+"F0.wireOp",EDGE,"E74.3.0.0");Q18=makeQuery(id+"F0.imprint","IMPRINT",FACE,{"disambiguationData":[TD([[makeQuery(id+"F0.imprint","IMPRINT",EDGE,{"derivedFrom":subQ0}),-1.0]])]});}
            var Q19;
            {var subQ0=sQuery(id+"F0.wireOp",EDGE,"E74.5.0.0");Q19=makeQuery(id+"F0.imprint","IMPRINT",FACE,{"disambiguationData":[TD([[makeQuery(id+"F0.imprint","IMPRINT",EDGE,{"derivedFrom":subQ0}),-1.0]])]});}
            var Q20;
            {var subQ0=sQuery(id+"F0.wireOp",EDGE,"E74.7.0.0");Q20=makeQuery(id+"F0.imprint","IMPRINT",FACE,{"disambiguationData":[TD([[makeQuery(id+"F0.imprint","IMPRINT",EDGE,{"derivedFrom":subQ0}),-1.0]])]});}
            extrude(context, id + "F8", {"entities" : qUnion([Q0, Q1, Q2, Q3, Q4, Q5, Q6, Q7, Q8, Q9, Q10, Q11, Q12, Q13, Q14, Q15, Q16, Q17, Q18, Q19, Q20]), "depth" : 100 * mm});
        }
        {
            var Q0;
            {var subQ0=sQuery(id+"F0.wireOp",EDGE,"E70");Q0=makeQuery(id+"F0.imprint","IMPRINT",FACE,{"disambiguationData":[TD([[makeQuery(id+"F0.imprint","IMPRINT",EDGE,{"derivedFrom":subQ0}),1.0]])]});}
            var Q1;
            {var subQ0=sQuery(id+"F0.wireOp",EDGE,"E71.2.0.0");Q1=makeQuery(id+"F0.imprint","IMPRINT",FACE,{"disambiguationData":[TD([[makeQuery(id+"F0.imprint","IMPRINT",EDGE,{"derivedFrom":subQ0}),1.0]])]});}
            var Q2;
            {var subQ0=sQuery(id+"F0.wireOp",EDGE,"E71.4.0.0");Q2=makeQuery(id+"F0.imprint","IMPRINT",FACE,{"disambiguationData":[TD([[makeQuery(id+"F0.imprint","IMPRINT",EDGE,{"derivedFrom":subQ0}),1.0]])]});}
            var Q3;
            {var subQ0=sQuery(id+"F0.wireOp",EDGE,"E71.6.0.0");Q3=makeQuery(id+"F0.imprint","IMPRINT",FACE,{"disambiguationData":[TD([[makeQuery(id+"F0.imprint","IMPRINT",EDGE,{"derivedFrom":subQ0}),1.0]])]});}
            var Q4;
            {var subQ0=sQuery(id+"F0.wireOp",EDGE,"E71.8.0.0");Q4=makeQuery(id+"F0.imprint","IMPRINT",FACE,{"disambiguationData":[TD([[makeQuery(id+"F0.imprint","IMPRINT",EDGE,{"derivedFrom":subQ0}),1.0]])]});}
            var Q5;
            {var subQ0=sQuery(id+"F0.wireOp",EDGE,"E73.1.0.0");Q5=makeQuery(id+"F0.imprint","IMPRINT",FACE,{"disambiguationData":[TD([[makeQuery(id+"F0.imprint","IMPRINT",EDGE,{"derivedFrom":subQ0}),1.0]])]});}
            var Q6;
            {var subQ0=sQuery(id+"F0.wireOp",EDGE,"E73.3.0.0");Q6=makeQuery(id+"F0.imprint","IMPRINT",FACE,{"disambiguationData":[TD([[makeQuery(id+"F0.imprint","IMPRINT",EDGE,{"derivedFrom":subQ0}),1.0]])]});}
            var Q7;
            {var subQ0=sQuery(id+"F0.wireOp",EDGE,"E73.5.0.0");Q7=makeQuery(id+"F0.imprint","IMPRINT",FACE,{"disambiguationData":[TD([[makeQuery(id+"F0.imprint","IMPRINT",EDGE,{"derivedFrom":subQ0}),1.0]])]});}
            var Q8;
            {var subQ0=sQuery(id+"F0.wireOp",EDGE,"E73.7.0.0");Q8=makeQuery(id+"F0.imprint","IMPRINT",FACE,{"disambiguationData":[TD([[makeQuery(id+"F0.imprint","IMPRINT",EDGE,{"derivedFrom":subQ0}),1.0]])]});}
            var Q9;
            {var subQ0=sQuery(id+"F0.wireOp",EDGE,"E61.right");Q9=makeQuery(id+"F0.imprint","IMPRINT",FACE,{"disambiguationData":[TD([[makeQuery(id+"F0.imprint","IMPRINT",EDGE,{"derivedFrom":subQ0}),-1.0]])]});}
            var Q10;
            {var subQ0=sQuery(id+"F0.wireOp",EDGE,"E72.2.0.0");Q10=makeQuery(id+"F0.imprint","IMPRINT",FACE,{"disambiguationData":[TD([[makeQuery(id+"F0.imprint","IMPRINT",EDGE,{"derivedFrom":subQ0}),-1.0]])]});}
            var Q11;
            {var subQ0=sQuery(id+"F0.wireOp",EDGE,"E72.4.0.0");Q11=makeQuery(id+"F0.imprint","IMPRINT",FACE,{"disambiguationData":[TD([[makeQuery(id+"F0.imprint","IMPRINT",EDGE,{"derivedFrom":subQ0}),-1.0]])]});}
            var Q12;
            {var subQ0=sQuery(id+"F0.wireOp",EDGE,"E72.6.0.0");Q12=makeQuery(id+"F0.imprint","IMPRINT",FACE,{"disambiguationData":[TD([[makeQuery(id+"F0.imprint","IMPRINT",EDGE,{"derivedFrom":subQ0}),-1.0]])]});}
            var Q13;
            {var subQ0=sQuery(id+"F0.wireOp",EDGE,"E72.8.0.0");Q13=makeQuery(id+"F0.imprint","IMPRINT",FACE,{"disambiguationData":[TD([[makeQuery(id+"F0.imprint","IMPRINT",EDGE,{"derivedFrom":subQ0}),-1.0]])]});}
            var Q14;
            {var subQ0=sQuery(id+"F0.wireOp",EDGE,"E74.1.0.0");Q14=makeQuery(id+"F0.imprint","IMPRINT",FACE,{"disambiguationData":[TD([[makeQuery(id+"F0.imprint","IMPRINT",EDGE,{"derivedFrom":subQ0}),-1.0]])]});}
            var Q15;
            {var subQ0=sQuery(id+"F0.wireOp",EDGE,"E74.3.0.0");Q15=makeQuery(id+"F0.imprint","IMPRINT",FACE,{"disambiguationData":[TD([[makeQuery(id+"F0.imprint","IMPRINT",EDGE,{"derivedFrom":subQ0}),-1.0]])]});}
            var Q16;
            {var subQ0=sQuery(id+"F0.wireOp",EDGE,"E74.5.0.0");Q16=makeQuery(id+"F0.imprint","IMPRINT",FACE,{"disambiguationData":[TD([[makeQuery(id+"F0.imprint","IMPRINT",EDGE,{"derivedFrom":subQ0}),-1.0]])]});}
            var Q17;
            {var subQ0=sQuery(id+"F0.wireOp",EDGE,"E74.7.0.0");Q17=makeQuery(id+"F0.imprint","IMPRINT",FACE,{"disambiguationData":[TD([[makeQuery(id+"F0.imprint","IMPRINT",EDGE,{"derivedFrom":subQ0}),-1.0]])]});}
            extrude(context, id + "F9", {"entities" : qUnion([Q0, Q1, Q2, Q3, Q4, Q5, Q6, Q7, Q8, Q9, Q10, Q11, Q12, Q13, Q14, Q15, Q16, Q17]), "depth" : 100 * mm});
        }
        {
            var Q0;
            {var subQ0=sQuery(id+"F0.wireOp",EDGE,"E74.8.0.0");Q0=makeQuery(id+"F0.imprint","IMPRINT",FACE,{"disambiguationData":[TD([[makeQuery(id+"F0.imprint","IMPRINT",EDGE,{"derivedFrom":subQ0}),-1.0]])]});}
            var Q1;
            {var subQ0=sQuery(id+"F0.wireOp",EDGE,"E74.6.0.0");Q1=makeQuery(id+"F0.imprint","IMPRINT",FACE,{"disambiguationData":[TD([[makeQuery(id+"F0.imprint","IMPRINT",EDGE,{"derivedFrom":subQ0}),-1.0]])]});}
            var Q2;
            {var subQ0=sQuery(id+"F0.wireOp",EDGE,"E74.4.0.0");Q2=makeQuery(id+"F0.imprint","IMPRINT",FACE,{"disambiguationData":[TD([[makeQuery(id+"F0.imprint","IMPRINT",EDGE,{"derivedFrom":subQ0}),-1.0]])]});}
            var Q3;
            {var subQ0=sQuery(id+"F0.wireOp",EDGE,"E74.2.0.0");Q3=makeQuery(id+"F0.imprint","IMPRINT",FACE,{"disambiguationData":[TD([[makeQuery(id+"F0.imprint","IMPRINT",EDGE,{"derivedFrom":subQ0}),-1.0]])]});}
            var Q4;
            {var subQ0=sQuery(id+"F0.wireOp",EDGE,"E72.9.0.0");Q4=makeQuery(id+"F0.imprint","IMPRINT",FACE,{"disambiguationData":[TD([[makeQuery(id+"F0.imprint","IMPRINT",EDGE,{"derivedFrom":subQ0}),-1.0]])]});}
            var Q5;
            {var subQ0=sQuery(id+"F0.wireOp",EDGE,"E72.7.0.0");Q5=makeQuery(id+"F0.imprint","IMPRINT",FACE,{"disambiguationData":[TD([[makeQuery(id+"F0.imprint","IMPRINT",EDGE,{"derivedFrom":subQ0}),-1.0]])]});}
            var Q6;
            {var subQ0=sQuery(id+"F0.wireOp",EDGE,"E72.5.0.0");Q6=makeQuery(id+"F0.imprint","IMPRINT",FACE,{"disambiguationData":[TD([[makeQuery(id+"F0.imprint","IMPRINT",EDGE,{"derivedFrom":subQ0}),-1.0]])]});}
            var Q7;
            {var subQ0=sQuery(id+"F0.wireOp",EDGE,"E72.3.0.0");Q7=makeQuery(id+"F0.imprint","IMPRINT",FACE,{"disambiguationData":[TD([[makeQuery(id+"F0.imprint","IMPRINT",EDGE,{"derivedFrom":subQ0}),-1.0]])]});}
            var Q8;
            {var subQ0=sQuery(id+"F0.wireOp",EDGE,"E72.1.0.0");Q8=makeQuery(id+"F0.imprint","IMPRINT",FACE,{"disambiguationData":[TD([[makeQuery(id+"F0.imprint","IMPRINT",EDGE,{"derivedFrom":subQ0}),-1.0]])]});}
            extrude(context, id + "F10", {"entities" : qUnion([Q0, Q1, Q2, Q3, Q4, Q5, Q6, Q7, Q8]), "depth" : 100 * mm});
        }
    });
